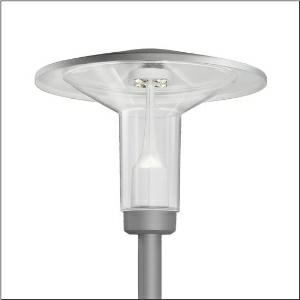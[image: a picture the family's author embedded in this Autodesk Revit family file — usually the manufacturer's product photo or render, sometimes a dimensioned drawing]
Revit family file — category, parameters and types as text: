
# Revit family: laterne_iq___st1_2a_5xa5255kf14h_a0c9
name_source: partatom
category: Lighting Fixtures
units: mm (PartAtom-declared; Revit-internal decimal feet)

## family parameters
Cut with Voids When Loaded = No
Host = Face
Light Source = No
Part Type = Normal
Room Calculation Point = No
Round Connector Dimension = Use Diameter
Shared = No

## types (1)
- --- (1 x LED, 1540 lm, 10 W, 4000K)
    Apparent Load = 10 VA
    CIE Flux Codes = 25 63 94 98 100
    Color Rendering = 70
    Color Temperature = 4000K
    Default Elevation = 1800 mm
    Description = Lantern iQ, mast luminaire, Module 540 iQ-SR, primary light control with 3 zone facetted reflector, of plastic, silver coated, highly specular, structured, primary optical cover: cover, of PMMA, transparent, light distribution: ST1.2a, light emission: direct distribution, primary light characteristic: asymmetric, installation type: post-top, LED, High Power LED, rated luminous flux: 1.540lm, luminous efficacy: 154lm/W, light colour: 740, colour temperature: 4000K, control gear: iQ Street-Remote, control: pre-setting: logarithmic dimming characteristic, Street-Remote, Auto-Match, Temp-Guard, Lumen-Switch, Night-Set, Smart-Wire, Light-Fading, Desk-Remote (wireless, voltage-free reading and setting of iQ features in the workshop via application-optimized NFC function/RFID function), optimised constant luminous flux control (CLO 2.0), with terminal, 6-pole, max. 2.5mm², mains connection: 230..240V, AC, 50/60Hz, start of lifetime: 10W, end of service life: 10W, reduction: 5W, luminaire housing, upper part, of glass-fibre reinforced polyester, coated, Siteco® metallic grey (DB 702S), diameter: 750mm, height: 583mm, spigot size: d x l = 76 x 70mm (post-top) | with reducer (optional accessory) 60 x 70mm, mounting height: 3..5m, post-top mast mounting element, of diecast aluminium, coated, Siteco® metallic grey (DB 702S), Module 540 iQ-SR, traffic white (RAL 9016), equipment: standard, protection rating (complete): IP65, insulation class (complete): insulation class II (safety insulation), certification: CE, ENEC, VDE, packaging unit: 1 piece

Light Distribution: ST1.2a
    Height = 583 mm
    Lamp = 1 x LED
    Lamp Light Flux = 1540 lm
    Lamp Power = 10 W
    Lamp count = 1
    Length = 750 mm
    Luminous efficacy = 154 lm/W
    Manufacturer = Siteco
    ModVariant = No
    Model = 5XA5255KF14H
    Number of Poles = 1
    OnlyDefault = Yes
    Power Factor = 1
    Product Name = Laterne iQ | ST1.2a
    Product group = mast luminaire | pylon top
    ProductGroupID = 6100
    Protection Class = Protection class II
    Protection Degree = IP 65
    RLX_Detail_Level = 1
    RLX_Emergency_Light_Flux = 0 lm
    RLX_Emergency_Type = 0
    RLX_Emergency_Type_DB = No
    RlxData = <blob elided: 107261 chars, md5=27c83849>
    Socket = socket
    Standby Power = 0 W
    System Light Flux = 1540 lm
    System Power = 10 W
    Type Comments = factory setting: luminous flux: 100 % | dim-lin: 254 | 401 mA
    Type Image = l_1006050.jpg
    URL = http://relux.com
    VarID = @adj_160081
    Voltage = 0 V
    Weight = 0.00 kg
    Width = 0 mm  [stored 0 ft]

note: [stored X ft] marks values corroborated as IEEE doubles in the binary element streams (Revit-internal decimal feet)

## geometry (parser evidence)
native form markers: Blend x4, Sweep x8
no freeform markers — native parametric forms only
